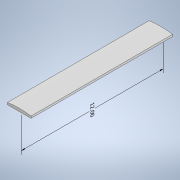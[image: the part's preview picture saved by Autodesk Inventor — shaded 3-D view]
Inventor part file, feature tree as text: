
AUTODESK INVENTOR PART (.ipt)
format: ipt  version: 2021.2 (Build 252289000, 289)  size: 103,424 bytes
history: native  units: in
note: dims shown in document units (in); Inventor stores cm internally (conversion verified against a paired STEP export)
features: other x2, extrude x1, sketch x1
ambient origin geometry x8: Origin, YZ Plane, XZ Plane, XY Plane, X Axis, Y Axis, Z Axis, Center Point
bodies: Solid1 (feature_tree)
feature tree (4):
  other  "Annotations"
  extrude  "Extrusion1"  Depth=1.0in
  sketch  "Sketch1"  dims[d0=1.0in d1=1.0in d2=6.25in d3=0.25in d4=12.0in d5=0.0in d6=0.2352in d7=0.1554in d8=12.0in]
  other  "Linear Dimension 1"
